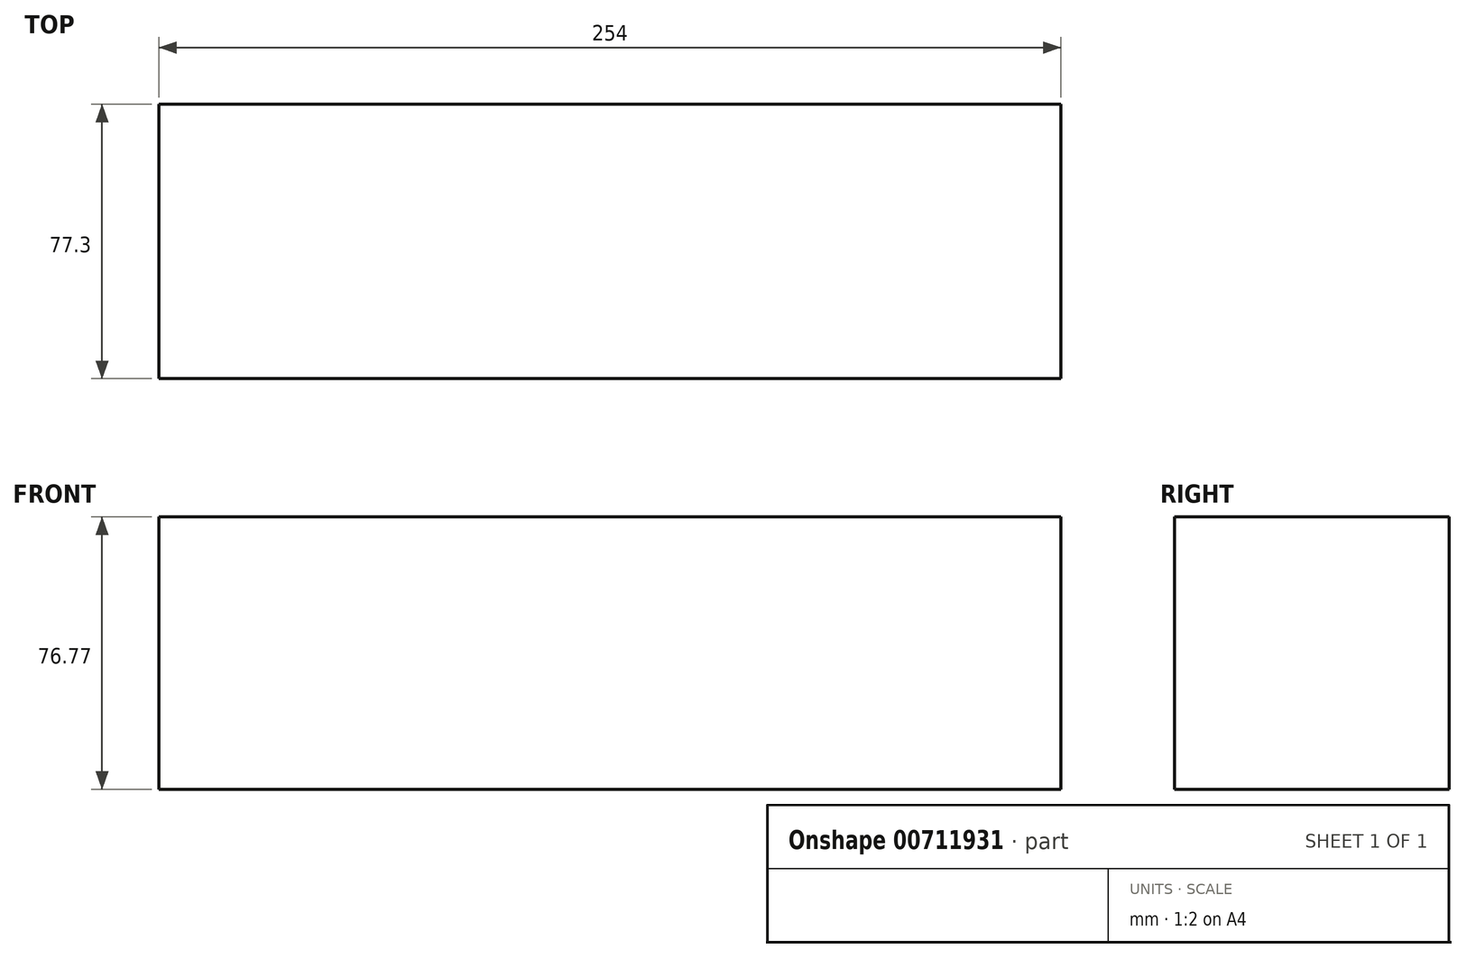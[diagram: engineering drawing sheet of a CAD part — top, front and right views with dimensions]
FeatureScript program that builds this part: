
annotation { "Feature Type Name" : "Feature", "Feature Type Description" : "" }
export const myFeature = defineFeature(function(context is Context, id is Id, definition is map)
    precondition{}
    {
        {
            var Q0;
            Q0=qCreatedBy(makeId("Right.planeOp"),FACE);
            var sketch = newSketch(context, id + "F0", { "sketchPlane" : qUnion([Q0])});
            skLineSegment(sketch, "E0.bottom", {"start": v(0, 0) * mm, "end": v(77.3, 0) * mm});
            skLineSegment(sketch, "E0.top", {"start": v(0, 76.77) * mm, "end": v(77.3, 76.77) * mm});
            skLineSegment(sketch, "E0.left", {"start": v(0, 0) * mm, "end": v(0, 76.77) * mm});
            skLineSegment(sketch, "E0.right", {"start": v(77.3, 0) * mm, "end": v(77.3, 76.77) * mm});
            skSolve(sketch);
        }
        {
            var Q0;
            Q0 = qSketchRegion(id + "F0", true);
            extrude(context, id + "F1", {"entities" : qUnion([Q0]), "depth" : 254 * mm, "offsetDistance" : 25.4 * mm});
        }
    });
